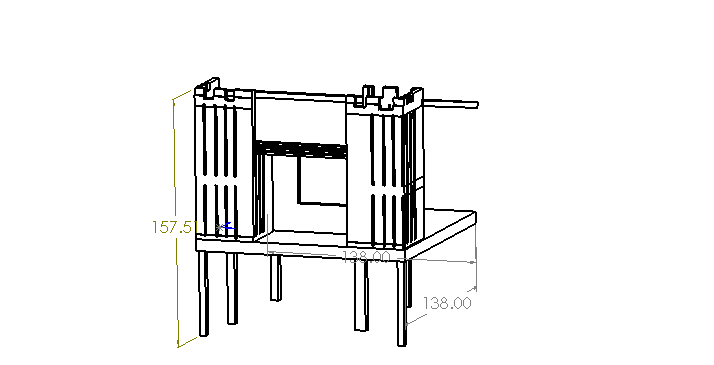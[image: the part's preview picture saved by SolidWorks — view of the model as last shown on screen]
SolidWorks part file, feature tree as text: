
SOLIDWORKS PART (.sldprt)
format: sldprt  version: not decoded by parser v0  size: 975,872 bytes
history: native  units: mm
features: sketch x17, extrude x9, cut_extrude x8, shell x1 + 1 further entry (+10 scaffold rows collapsed)
feature tree (46):
  "Annotations"  RD1=4000.681424mm RD2=3505.2mm RD3=3505.2mm
  scaffold x10  (default folders/planes/origin — collapsed)
  sketch  "Sketch1"  dims[D1=2438.4mm D2=2489.2mm D3=~106.659775mm]
  extrude  "Extrude1"  Depth=1676.4mm
  sketch  "Sketch2"  dims[D1=457.2mm]
  extrude  "Extrude2"  [1 undecoded]
  shell  "Shell1"  Thickness=88.9mm
  sketch  "Sketch5"  dims[D1=609.6mm D2=609.6mm D3=88.9mm]
  extrude  "Extrude3"  Depth=38.1mm
  sketch  "Sketch6"  dims[D1=3505.2mm D2=3505.2mm D3=38.1mm]
  extrude  "Extrude4"  Depth=190.5mm
  sketch  "Sketch7"  dims[D1=609.6mm D2=304.8mm D3=38.1mm D4=1371.6mm D5=914.4mm D6=609.6mm D7=304.8mm]
  cut_extrude  "Cut-Extrude1"  [1 undecoded]
  sketch  "Sketch8"  dims[D1=914.4mm D2=76.2mm D3=254.0mm D4=457.2mm]
  cut_extrude  "Cut-Extrude2"  [1 undecoded]
  sketch  "Sketch9"  dims[D1=101.6mm D2=101.6mm D3=38.1mm D4=38.1mm D5=38.1mm D6=38.1mm]
  extrude  "Extrude5"  Depth=1371.6mm
  sketch  "Sketch10"  dims[c1.D1=965.2mm c1.D2=965.2mm c1.D3=88.9mm c1.D4=88.9mm c2.D3=88.9mm c2.D4=88.9mm]
  extrude  "Extrude6"  Depth=2438.4mm
  sketch  "Sketch11"
  cut_extrude  "Cut-Extrude3"  [1 undecoded]
  sketch  "Sketch12"
  cut_extrude  "Cut-Extrude4"  [1 undecoded]
  sketch  "Sketch13"
  cut_extrude  "Cut-Extrude5"  [1 undecoded]
  sketch  "Sketch15"
  cut_extrude  "Cut-Extrude6"  [1 undecoded]
  sketch  "Sketch19"  dims[D1=457.2mm]
  extrude  "Extrude9"  [1 undecoded]
  sketch  "Sketch20"  dims[D1=152.4mm D2=152.4mm]
  extrude  "Extrude10"  Depth=88.9mm
  sketch  "Sketch21"  dims[D1=914.4mm]
  cut_extrude  "Cut-Extrude9"  [1 undecoded]
  sketch  "Sketch22"  dims[D1=914.4mm]
  cut_extrude  "Cut-Extrude10"  [1 undecoded]
  sketch  "Sketch23"
  extrude  "Extrude11"  Depth=38.1mm
decode coverage: 20 of 35 modeling features carry decoded parameters; 1 rows unclassified (native names shown)
note: ~ marks probable driven/reference dimensions
note: 10 parameter values undecoded
summary: no parameter record found for 10 features
note: suppression state not decoded; provenance and decode notes live in map.json
